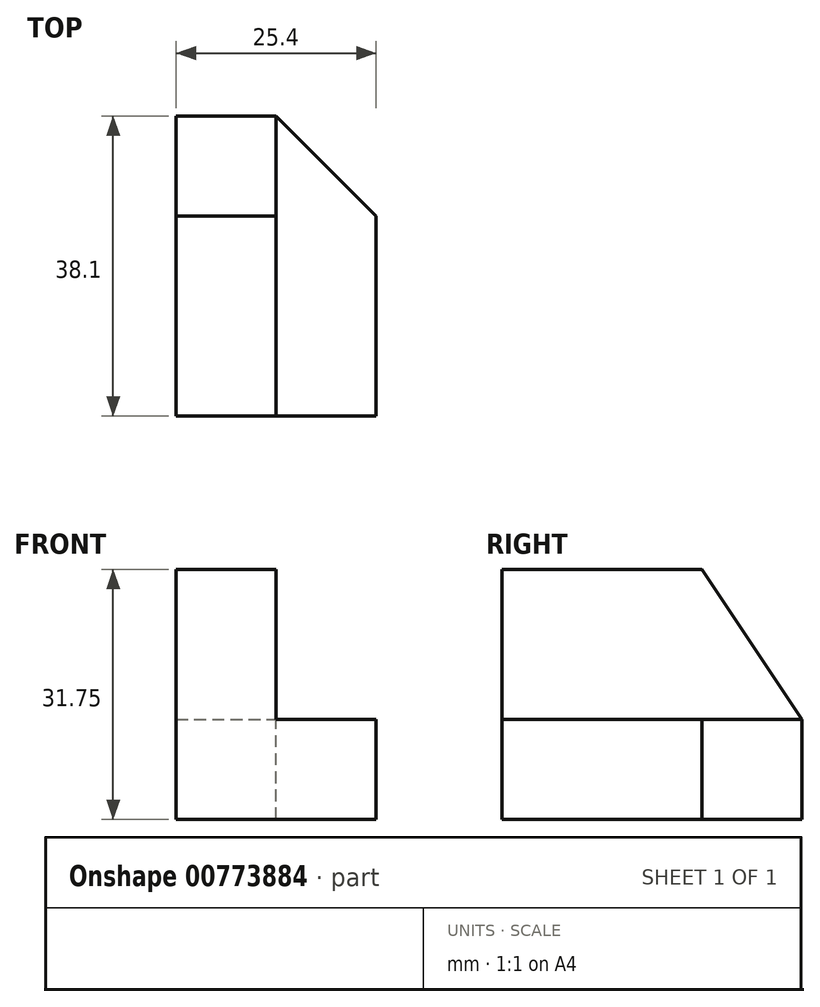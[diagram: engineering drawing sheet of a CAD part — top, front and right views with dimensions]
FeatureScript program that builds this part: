
annotation { "Feature Type Name" : "Feature", "Feature Type Description" : "" }
export const myFeature = defineFeature(function(context is Context, id is Id, definition is map)
    precondition{}
    {
        {
            var Q0;
            Q0=qCreatedBy(makeId("Right.planeOp"),FACE);
            var sketch = newSketch(context, id + "F0", { "sketchPlane" : qUnion([Q0])});
            skLineSegment(sketch, "E0", {"start": v(0, 0) * mm, "end": v(0, 31.75) * mm});
            skLineSegment(sketch, "E1", {"start": v(0, 0) * mm, "end": v(38.1, 0) * mm});
            skLineSegment(sketch, "E2", {"start": v(38.1, 0) * mm, "end": v(38.1, 31.75) * mm});
            skLineSegment(sketch, "E3", {"start": v(38.1, 31.75) * mm, "end": v(0, 31.75) * mm});
            skSolve(sketch);
        }
        {
            var Q0;
            Q0=makeQuery(id+"F0.imprint","IMPRINT",FACE,{"disambiguationData":[TD([[makeQuery(id+"F0.imprint","IMPRINT",EDGE,{"derivedFrom":sQuery(id+"F0.wireOp",EDGE,"E0")}),-1.0]])]});
            extrude(context, id + "F1", {"entities" : qUnion([Q0]), "depth" : 25.4 * mm, "offsetDistance" : 25.4 * mm});
        }
        {
            var Q0;
            Q0=makeQuery(id+"F1.opExtrude","SWEPT_FACE",FACE,{"disambiguationData":[OSD([sQuery(id+"F0.wireOp",EDGE,"E0")])]});
            var sketch = newSketch(context, id + "F2", { "sketchPlane" : qUnion([Q0])});
            skLineSegment(sketch, "E4", {"start": v(25.4, 0) * mm, "end": v(25.4, 12.7) * mm});
            skLineSegment(sketch, "E5", {"start": v(25.4, 12.7) * mm, "end": v(12.7, 12.7) * mm});
            skLineSegment(sketch, "E6", {"start": v(12.7, 12.7) * mm, "end": v(12.7, 31.75) * mm});
            skSolve(sketch);
        }
        {
            var Q0;
            {var subQ0=sQuery(id+"F2.wireOp",EDGE,"E5");Q0=makeQuery(id+"F2.imprint","IMPRINT",FACE,{"disambiguationData":[TD([[makeQuery(id+"F2.imprint","IMPRINT",EDGE,{"derivedFrom":subQ0}),-1.0]])]});}
            extrude(context, id + "F3", {"entities" : qUnion([Q0]), "operationType" : NewBodyOperationType.REMOVE, "oppositeDirection" : true, "depth" : 38.1 * mm, "offsetDistance" : 25.4 * mm});
        }
        {
            var Q0;
            Q0=makeQuery(id+"F3.boolean.opBoolean","COPY",FACE,{"derivedFrom":makeQuery(id+"F3.opExtrude","SWEPT_FACE",FACE,{"disambiguationData":[OSD([sQuery(id+"F2.wireOp",EDGE,"E6")])]})});
            var sketch = newSketch(context, id + "F4", { "sketchPlane" : qUnion([Q0])});
            skLineSegment(sketch, "E7", {"start": v(0, 31.75) * mm, "end": v(25.4, 31.75) * mm});
            skLineSegment(sketch, "E8", {"start": v(25.4, 31.75) * mm, "end": v(38.1, 12.7) * mm});
            skSolve(sketch);
        }
        {
            var Q0;
            {var subQ0=sQuery(id+"F4.wireOp",EDGE,"E8");Q0=makeQuery(id+"F4.imprint","IMPRINT",FACE,{"disambiguationData":[TD([[makeQuery(id+"F4.imprint","IMPRINT",EDGE,{"derivedFrom":subQ0}),1.0]])]});}
            extrude(context, id + "F5", {"entities" : qUnion([Q0]), "operationType" : NewBodyOperationType.REMOVE, "oppositeDirection" : true, "depth" : 25.4 * mm, "offsetDistance" : 25.4 * mm});
        }
        {
            var Q0;
            Q0=makeQuery(id+"F3.boolean.opBoolean","COPY",FACE,{"derivedFrom":makeQuery(id+"F3.opExtrude","SWEPT_FACE",FACE,{"disambiguationData":[OSD([sQuery(id+"F2.wireOp",EDGE,"E5")])]})});
            var sketch = newSketch(context, id + "F6", { "sketchPlane" : qUnion([Q0])});
            skLineSegment(sketch, "E9", {"start": v(25.4, 0) * mm, "end": v(25.4, 25.4) * mm});
            skLineSegment(sketch, "E10", {"start": v(12.7, 38.1) * mm, "end": v(25.4, 25.4) * mm});
            skSolve(sketch);
        }
        {
            var Q0;
            {var subQ0=sQuery(id+"F6.wireOp",EDGE,"E10");Q0=makeQuery(id+"F6.imprint","IMPRINT",FACE,{"disambiguationData":[TD([[makeQuery(id+"F6.imprint","IMPRINT",EDGE,{"derivedFrom":subQ0}),1.0]])]});}
            extrude(context, id + "F7", {"entities" : qUnion([Q0]), "operationType" : NewBodyOperationType.REMOVE, "oppositeDirection" : true, "depth" : 25.4 * mm, "offsetDistance" : 25.4 * mm});
        }
    });
